# Revit family: Waste_Receptacle-Bradley_Corp-3157
name_source: partatom
category: Specialty Equipment
revit_build: Autodesk Revit MEP 2012 (Build: 20110309_2315(x64)
units: mm (PartAtom-declared; Revit-internal decimal feet)

## types (2) — shared parameters
ADA Compliant = Yes
Assembly Code = E1090200
Buy American Act = Yes
Cabinet Material = Bradley Corp Stainless Steel - Satin
Default Elevation = 44"
Depth = 6 3/4"
Height = 49 1/4"
MasterFormat Number = 12 46 33
MasterFormat Title = Waste Receptacles
OmniClass Table 21 Number = 21-03 10 90 40
OmniClass Table 21 Title = Toilet, Bath, and Laundry Accessories
OmniClass Table 23 Number = 23-21 43 23 11
OmniClass Table 23 Title = Installed Sanitary Waste Receptacles
Product Tech Data URL - English = http://bradleycorp.com
Specifications URL = http://www.bradleycorp.com
URL = http://www.bradleycorp.com
Version = 2.0
Warranty Information = Complete unit, excepting mirrors warranted for one year.
 Stainless steel mirror frames for fifteen years.
 Plate glass mirrors for fifteen years.
 This warranty does not cover installation or any other labor charges and does not apply to any units,
 which have been damaged by accident, abuse, improper installation, improper maintenance, or altered in any way.
Width = 14 1/4"

## per-type parameters (varying)
| type | Collar Depth Adjuster | Collar Visibility | Depth of which projects | Description | Manufacturer | Model | Wall Opening Depth |
| Recessed | 1/2" | No | 1/2" | Waste Receptacle, 9.2 Gallon, Recessed | Bradley Corporation | 3157-000000 | 6 1/2" |
| Semi-Recessed | 3 3/4" | Yes | 3 3/4" | Waste Receptacle, 9.2 Gallon, Semi-Recessed | Bradley Corp | 3157-100000 | 3" |

note: column(s) folded — value = type name in every type: Type Comments

## geometry (parser evidence)
native form markers: Blend x2, Sweep x1
no freeform markers — native parametric forms only
